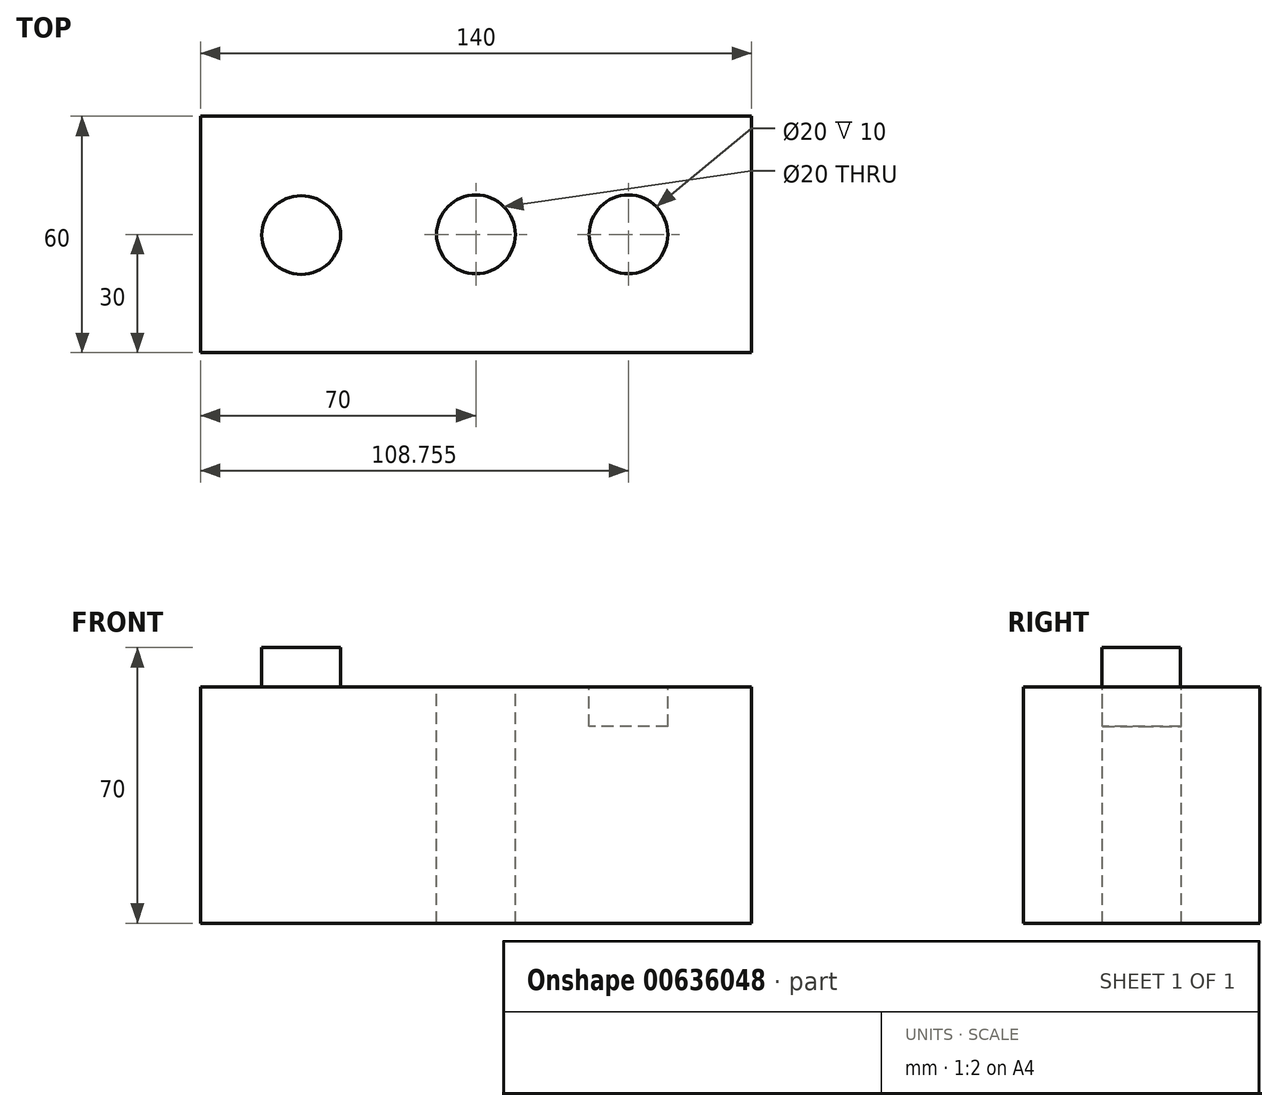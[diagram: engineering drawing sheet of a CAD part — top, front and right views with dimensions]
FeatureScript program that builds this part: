
annotation { "Feature Type Name" : "Feature", "Feature Type Description" : "" }
export const myFeature = defineFeature(function(context is Context, id is Id, definition is map)
    precondition{}
    {
        {
            var Q0;
            Q0=qCreatedBy(makeId("Top.planeOp"),FACE);
            var sketch = newSketch(context, id + "F0", { "sketchPlane" : qUnion([Q0])});
            skLineSegment(sketch, "E0.bottom", {"start": v(70, -30) * mm, "end": v(-70, -30) * mm});
            skLineSegment(sketch, "E0.top", {"start": v(70, 30) * mm, "end": v(-70, 30) * mm});
            skLineSegment(sketch, "E0.left", {"start": v(70, -30) * mm, "end": v(70, 30) * mm});
            skLineSegment(sketch, "E0.right", {"start": v(-70, -30) * mm, "end": v(-70, 30) * mm});
            skPoint(sketch, "E0.middle", {"position": v(0, 0) * mm});
            skSolve(sketch);
        }
        {
            var Q0;
            Q0 = qSketchRegion(id + "F0", true);
            extrude(context, id + "F1", {"entities" : qUnion([Q0]), "depth" : 60 * mm, "offsetDistance" : 25 * mm});
        }
        {
            var Q0;
            Q0=makeQuery(id+"F1.opExtrude","CAP_FACE",FACE,{"disambiguationData":[OSD([sQuery(id+"F0.wireOp",EDGE,"E0.bottom"),sQuery(id+"F0.wireOp",EDGE,"E0.top"),sQuery(id+"F0.wireOp",EDGE,"E0.left"),sQuery(id+"F0.wireOp",EDGE,"E0.right")])],"isStart":false});
            var sketch = newSketch(context, id + "F2", { "sketchPlane" : qUnion([Q0])});
            skLineSegment(sketch, "E1", {"start": v(-70, 0) * mm, "end": v(-50, 0) * mm});
            skLineSegment(sketch, "E2", {"start": v(70, 0) * mm, "end": v(50, 0) * mm});
            skPoint(sketch, "E2.endSnap0", {"position": v(70, 0) * mm});
            skSolve(sketch);
        }
        {
            var Q0;
            {var subQ3=makeQuery(id+"F1.opExtrude","CAP_EDGE",EDGE,{"disambiguationData":[OSD([sQuery(id+"F0.wireOp",EDGE,"E0.bottom")])],"isStart":false});Q0=makeQuery(id+"F2.imprint","IMPRINT",FACE,{"disambiguationData":[TD([[makeQuery(id+"F2.imprint","IMPRINT",EDGE,{"derivedFrom":subQ3}),-1.0]])]});}
            var sketch = newSketch(context, id + "F3", { "sketchPlane" : qUnion([Q0])});
            skCircle(sketch, "E3", {"center": v(-44.4, -0.15) * mm, "radius": 10 * mm});
            skPoint(sketch, "E3.first.point", {"position": v(-54.4, 0) * mm});
            skPoint(sketch, "E3.second.point", {"position": v(-34.4, 0) * mm});
            skPoint(sketch, "E3.third.point", {"position": v(-44.24, -10.15) * mm});
            skSolve(sketch);
        }
        {
            var Q0;
            {var subQ3=makeQuery(id+"F1.opExtrude","CAP_EDGE",EDGE,{"disambiguationData":[OSD([sQuery(id+"F0.wireOp",EDGE,"E0.bottom")])],"isStart":false});Q0=makeQuery(id+"F2.imprint","IMPRINT",FACE,{"disambiguationData":[TD([[makeQuery(id+"F2.imprint","IMPRINT",EDGE,{"derivedFrom":subQ3}),-1.0]])]});}
            var sketch = newSketch(context, id + "F4", { "sketchPlane" : qUnion([Q0])});
            skCircle(sketch, "E4", {"center": v(38.75, 0) * mm, "radius": 10 * mm});
            skPoint(sketch, "E4.first.point", {"position": v(48.75, 0) * mm});
            skPoint(sketch, "E4.second.point", {"position": v(28.75, 0) * mm});
            skPoint(sketch, "E4.third.point", {"position": v(38.47, -10) * mm});
            skSolve(sketch);
        }
        {
            var Q0;
            {var subQ3=makeQuery(id+"F1.opExtrude","CAP_EDGE",EDGE,{"disambiguationData":[OSD([sQuery(id+"F0.wireOp",EDGE,"E0.bottom")])],"isStart":false});Q0=makeQuery(id+"F2.imprint","IMPRINT",FACE,{"disambiguationData":[TD([[makeQuery(id+"F2.imprint","IMPRINT",EDGE,{"derivedFrom":subQ3}),-1.0]])]});}
            var sketch = newSketch(context, id + "F5", { "sketchPlane" : qUnion([Q0])});
            skCircle(sketch, "E5", {"center": v(0, 0) * mm, "radius": 10 * mm});
            skSolve(sketch);
        }
        {
            var Q0;
            Q0 = qSketchRegion(id + "F3", true);
            extrude(context, id + "F6", {"entities" : qUnion([Q0]), "operationType" : NewBodyOperationType.ADD, "depth" : 10 * mm, "offsetDistance" : 25 * mm});
        }
        {
            var Q0;
            Q0 = qSketchRegion(id + "F4", true);
            extrude(context, id + "F7", {"entities" : qUnion([Q0]), "operationType" : NewBodyOperationType.REMOVE, "oppositeDirection" : true, "depth" : 10 * mm, "offsetDistance" : 25 * mm});
        }
        {
            var Q0;
            Q0 = qSketchRegion(id + "F5", true);
            extrude(context, id + "F8", {"entities" : qUnion([Q0]), "operationType" : NewBodyOperationType.REMOVE, "oppositeDirection" : true, "depth" : 100.9 * mm, "offsetDistance" : 25 * mm});
        }
    });
